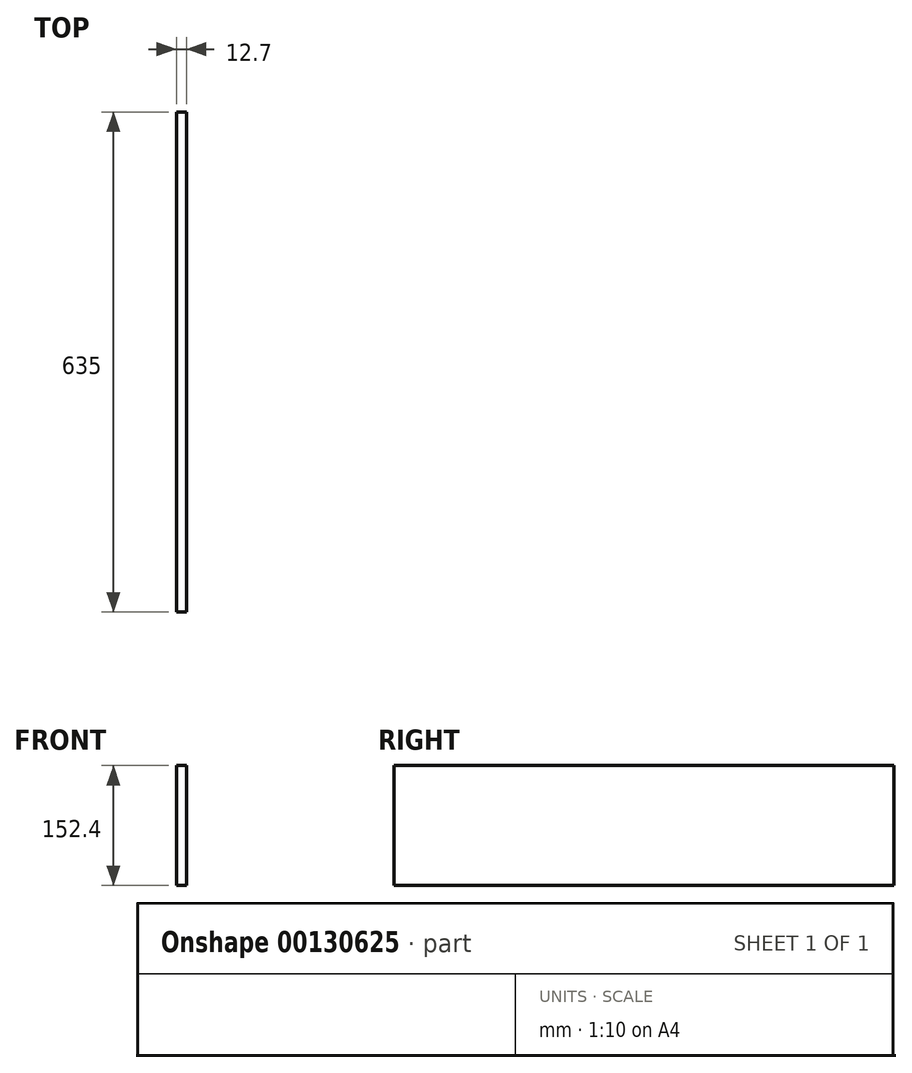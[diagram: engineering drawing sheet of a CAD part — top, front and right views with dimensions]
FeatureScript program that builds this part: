
annotation { "Feature Type Name" : "Feature", "Feature Type Description" : "" }
export const myFeature = defineFeature(function(context is Context, id is Id, definition is map)
    precondition{}
    {
        {
            var Q0;
            Q0=qCreatedBy(makeId("Right.planeOp"),FACE);
            var sketch = newSketch(context, id + "F0", { "sketchPlane" : qUnion([Q0])});
            skLineSegment(sketch, "E0.bottom", {"start": v(0, 0) * mm, "end": v(635, 0) * mm});
            skLineSegment(sketch, "E0.top", {"start": v(0, 152.4) * mm, "end": v(635, 152.4) * mm});
            skLineSegment(sketch, "E0.left", {"start": v(0, 0) * mm, "end": v(0, 152.4) * mm});
            skLineSegment(sketch, "E0.right", {"start": v(635, 0) * mm, "end": v(635, 152.4) * mm});
            skSolve(sketch);
        }
        {
            var Q0;
            Q0=makeQuery(id+"F0.imprint","IMPRINT",FACE,{"disambiguationData":[TD([[makeQuery(id+"F0.imprint","IMPRINT",EDGE,{"derivedFrom":sQuery(id+"F0.wireOp",EDGE,"E0.bottom")}),1.0]])]});
            extrude(context, id + "F1", {"entities" : qUnion([Q0]), "depth" : 12.7 * mm});
        }
    });
